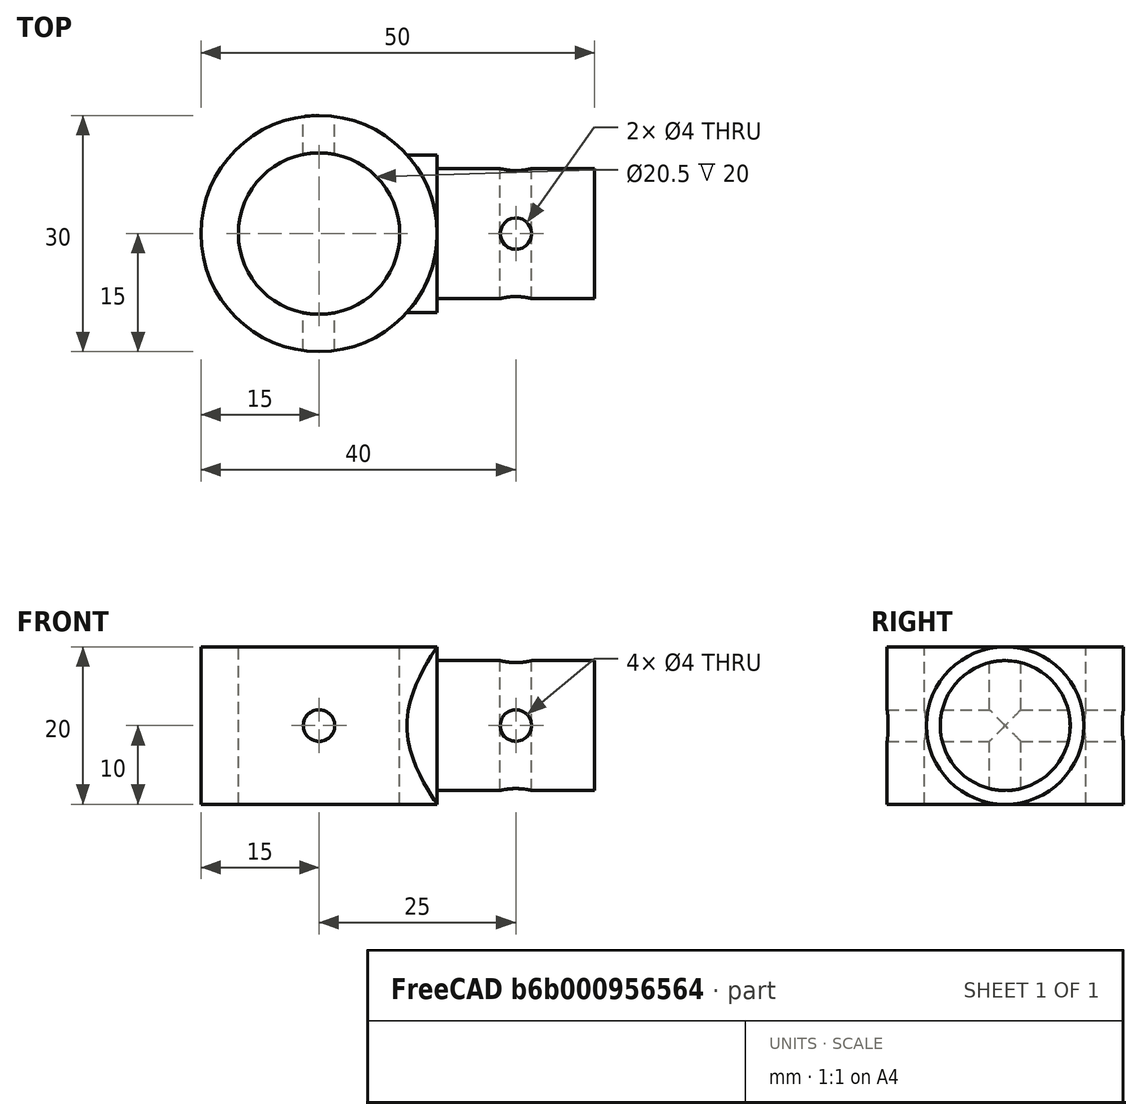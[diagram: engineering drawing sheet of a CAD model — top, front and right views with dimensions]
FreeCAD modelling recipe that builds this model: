
FCSTD DOCUMENT  (FreeCAD 0.18R16110 (Git))
Label: BaseT
License: All rights reserved
LicenseURL: http://en.wikipedia.org/wiki/All_rights_reserved
objects: Part::Cylinder×7, Part::MultiFuse×2, Part::Cut×1
note: 10 computed .brp shape members not serialized (recipe doc carries the construction recipe); baked Part::Feature solids carry a one-line shape summary decoded from their .brp

FEATURE [Part::Cylinder] Cylinder
  Angle = 360
  AttacherType = Attacher::AttachEngine3D
  Height = 20
  Placement = pos=(0,0,-10) rot=(0,0,1;0rad)
  Radius = 15
FEATURE [Part::Cylinder] Cylinder001
  Angle = 360
  AttacherType = Attacher::AttachEngine3D
  Height = 20
  Placement = pos=(0,0,-10) rot=(0,0,1;0rad)
  Radius = 10.25
FEATURE [Part::Cylinder] Cylinder002
  Angle = 360
  AttacherType = Attacher::AttachEngine3D
  Height = 5
  Placement = pos=(10,0,2.2e-15) rot=(0,1,0;1.5708rad)
  Radius = 10
FEATURE [Part::Cylinder] Cylinder003
  Angle = 360
  AttacherType = Attacher::AttachEngine3D
  Height = 20
  Placement = pos=(15,0,3.3e-15) rot=(0,1,0;1.5708rad)
  Radius = 8.25
FEATURE [Part::MultiFuse] Fusion  label="Positive Fusion"
  Shapes = -> [Cylinder,Cylinder002,Cylinder003]
FEATURE [Part::Cylinder] Cylinder004
  Angle = 360
  AttacherType = Attacher::AttachEngine3D
  Height = 30
  Placement = pos=(0,-15,3.3e-15) rot=(1,0,0;4.71239rad)
  Radius = 2
FEATURE [Part::Cylinder] Cylinder005
  Angle = 360
  AttacherType = Attacher::AttachEngine3D
  Height = 30
  Placement = pos=(25,0,-15) rot=(0,0,1;0rad)
  Radius = 2
FEATURE [Part::Cylinder] Cylinder006
  Angle = 360
  AttacherType = Attacher::AttachEngine3D
  Height = 30
  Placement = pos=(25,-15,3e-15) rot=(-1,0,0;1.5708rad)
  Radius = 2
FEATURE [Part::MultiFuse] Fusion001  label="Negative Fusion"
  Shapes = -> [Cylinder006,Cylinder005,Cylinder004,Cylinder001]
FEATURE [Part::Cut] Cut
  Base = -> Fusion
  Tool = -> Fusion001
